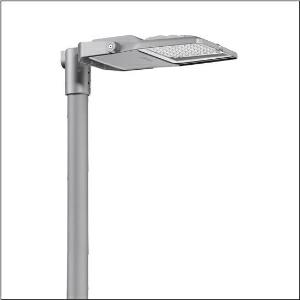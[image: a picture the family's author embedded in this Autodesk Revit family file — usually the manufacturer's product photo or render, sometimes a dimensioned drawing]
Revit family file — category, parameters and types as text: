
# Revit family: floodlight_fl_21_mini___pl64_5xa7775c2e3a_8880
name_source: partatom
category: Lighting Fixtures
units: mm (PartAtom-declared; Revit-internal decimal feet)

## family parameters
Cut with Voids When Loaded = No
Host = Face
Light Source = No
Part Type = Normal
Room Calculation Point = No
Round Connector Dimension = Use Diameter
Shared = No

## types (1)
- --- (1 x LED, 11770 lm, 89 W, 3000K)
    Apparent Load = 89 VA
    CIE Flux Codes = 28 80 98 100 100
    Color Rendering = 70
    Color Temperature = 3000K
    Default Elevation = 1800 mm
    Description = Floodlight FL 21 mini, floodlight, primary light control with lens, of PMMA, primary optical cover: protective disc, of toughened safety glass, transparent, light distribution: PL64, light emission: direct distribution, installation type: surface-mounted, LED, High Power LED, rated luminous flux: 11.770lm, luminous efficacy: 132lm/W, light colour: 730, colour temperature: 3000K, control: flexible luminous flux parameterisation, time-dependent luminous flux control, constant luminous flux control, overheat protection, pre-setting: logarithmic dimming characteristic, with terminal, 6-pole, mains connection: 220..240V, AC, 50/60Hz, start of lifetime: 89W, end of service life: 94W, reduction: 43W, luminaire housing, of diecast aluminium, powder-coated, Siteco® metallic grey (DB 702S), corrosivity category C5 mid according to DIN EN ISO 12944, sealing non-destructively replaceable, please order mast flange separately, mast bracket, of steel, galvanised, powder-coated, Siteco® metallic grey (DB 702S), Smart Interface above, protection rating (complete): IP66, insulation class (complete): insulation class II (safety insulation), certification: CE, ENEC, VDE, protection symbol: D, impact resistance: IK08, permissible operating ambient temperature: -40..+40°C, permissible operating ambient temperature for outdoor applications: -40..+50°C, standard: DIN EN 12944, LABS conformity tested according to VDMA 24364:2018-05, packaging unit: 1 piece

Light Distribution: PL64
    Height = 70 mm
    Lamp = 1 x LED
    Lamp Light Flux = 11770 lm
    Lamp Power = 89 W
    Lamp count = 1
    Length = 485 mm
    Luminous efficacy = 132 lm/W
    Manufacturer = Siteco
    ModVariant = No
    Model = 5XA7775C2E3A
    Number of Poles = 1
    OnlyDefault = Yes
    Power Factor = 1
    Product Name = Floodlight FL 21 mini | PL64
    Product group = floodlight | pylon annexe
    ProductGroupID = 6200
    Protection Class = Protection class II
    Protection Degree = IP 66
    RLX_Detail_Level = 1
    RLX_Emergency_Light_Flux = 0 lm
    RLX_Emergency_Type = 0
    RLX_Emergency_Type_DB = No
    RlxData = <blob elided: 100965 chars, md5=8fdc957b>
    Socket = socket
    Standby Power = 0 W
    System Light Flux = 11770 lm
    System Power = 89 W
    Type Comments = factory setting: luminous flux: 100 % | dim-lin: 254 | 456 mA
    Type Image = l_1007125.jpg
    URL = http://relux.com
    VarID = @adj_135745
    Voltage = 0 V
    Weight = 0.00 kg
    Width = 337 mm

## geometry (parser evidence)
native form markers: Blend x4, Sweep x12
no freeform markers — native parametric forms only
